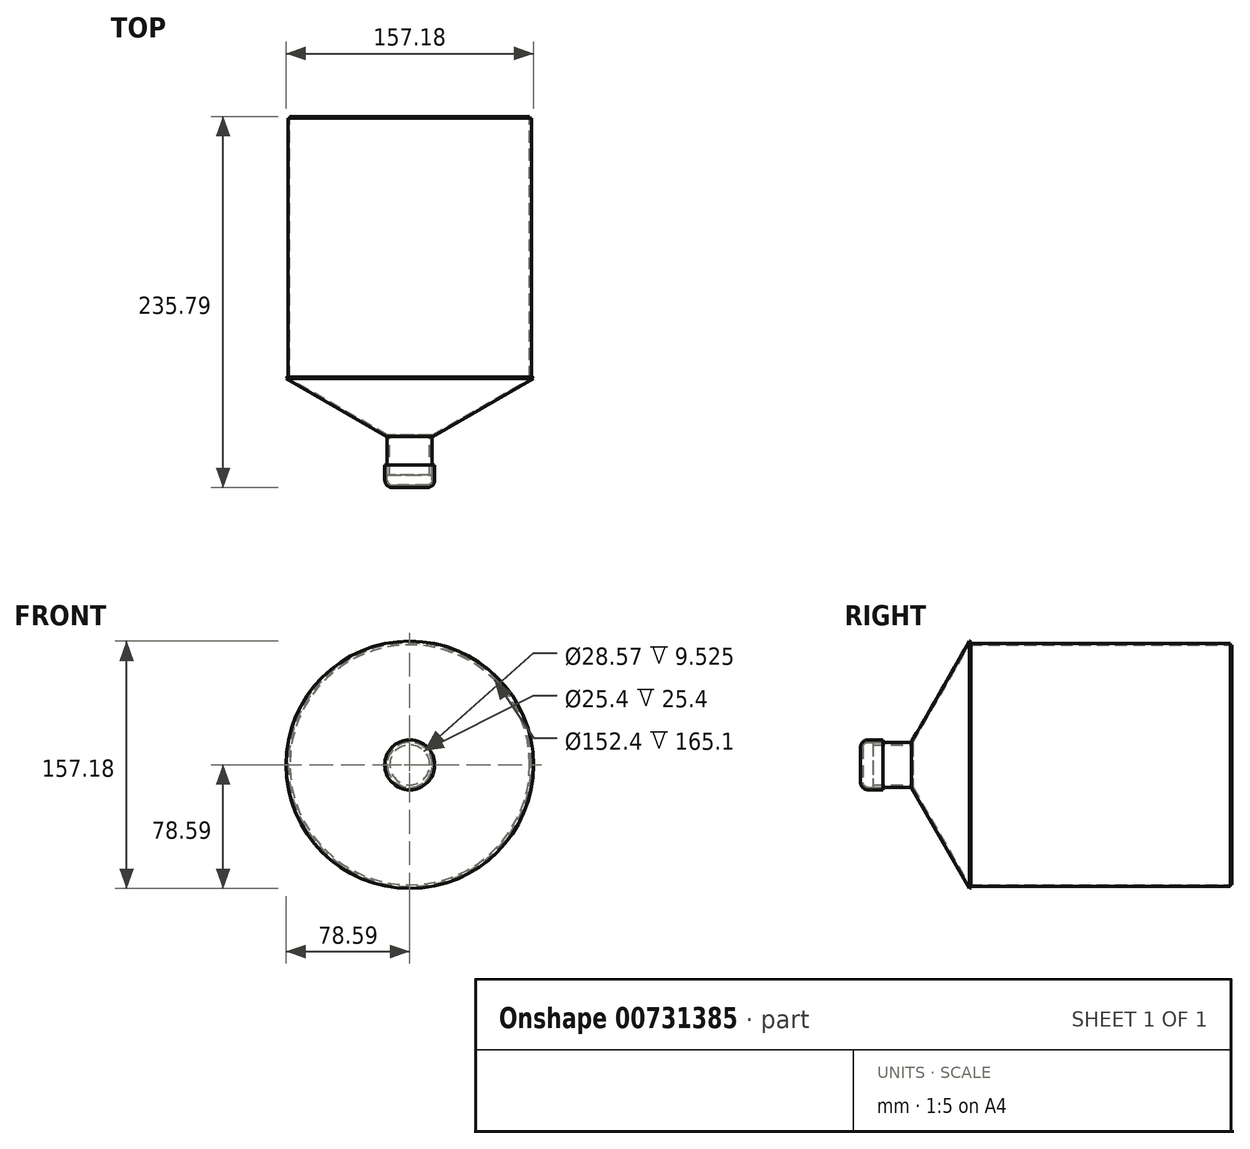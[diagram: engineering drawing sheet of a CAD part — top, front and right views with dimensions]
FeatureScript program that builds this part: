
annotation { "Feature Type Name" : "Feature", "Feature Type Description" : "" }
export const myFeature = defineFeature(function(context is Context, id is Id, definition is map)
    precondition{}
    {
        {
            var Q0;
            Q0=qCreatedBy(makeId("Front.planeOp"),FACE);
            var sketch = newSketch(context, id + "F0", { "sketchPlane" : qUnion([Q0])});
            skCircle(sketch, "E0", {"center": v(0, 0) * mm, "radius": 76.2 * mm});
            skCircle(sketch, "E1.0", {"center": v(0, 0) * mm, "radius": 77.22 * mm});
            skSolve(sketch);
        }
        {
            var Q0;
            Q0 = qSketchRegion(id + "F0", true);
            extrude(context, id + "F1", {"entities" : qUnion([Q0]), "depth" : 165.1 * mm, "offsetDistance" : 25.4 * mm});
        }
        {
            var Q0;
            Q0=makeQuery(id+"F0.imprint","IMPRINT",FACE,{"disambiguationData":[TD([[makeQuery(id+"F0.imprint","IMPRINT",EDGE,{"derivedFrom":sQuery(id+"F0.wireOp",EDGE,"E0")}),1.0]])]});
            extrude(context, id + "F2", {"entities" : qUnion([Q0]), "oppositeDirection" : true, "depth" : 1.02 * mm, "offsetDistance" : 25.4 * mm});
        }
        {
            var Q0;
            Q0=qCreatedBy(makeId("Right.planeOp"),FACE);
            var sketch = newSketch(context, id + "F3", { "sketchPlane" : qUnion([Q0])});
            skLineSegment(sketch, "E2", {"start": v(0, 0) * mm, "end": v(-195.69, 0) * mm, "construction": true});
            skLineSegment(sketch, "E3", {"start": v(-164.6, 78.08) * mm, "end": v(-201.43, 14.29) * mm});
            skPoint(sketch, "E4", {"position": v(-165.1, 77.22) * mm});
            skLineSegment(sketch, "E5.0", {"start": v(-165.48, 78.59) * mm, "end": v(-202.31, 14.8) * mm});
            skLineSegment(sketch, "E6", {"start": v(-202.31, 14.8) * mm, "end": v(-201.43, 14.29) * mm});
            skLineSegment(sketch, "E7", {"start": v(-165.48, 78.59) * mm, "end": v(-164.6, 78.08) * mm});
            skSolve(sketch);
        }
        {
            var Q0;
            Q0 = qSketchRegion(id + "F3", true);
            var Q1;
            Q1=sQuery(id+"F3.wireOp",EDGE,"E2");
            revolve(context, id + "F4", {"surfaceOperationType" : NewSurfaceOperationType.NEW, "entities" : qUnion([Q0]), "axis" : qUnion([Q1]), "revolveType" : RevolveType.FULL});
        }
        {
            var Q0;
            Q0=qCreatedBy(makeId("Right.planeOp"),FACE);
            var sketch = newSketch(context, id + "F5", { "sketchPlane" : qUnion([Q0])});
            skLineSegment(sketch, "E8", {"start": v(-1.93, 0) * mm, "end": v(-255.52, 0) * mm, "construction": true});
            skLineSegment(sketch, "E9", {"start": v(-201.43, 14.29) * mm, "end": v(-226.83, 14.29) * mm});
            skPoint(sketch, "E10", {"position": v(-201.43, 14.29) * mm});
            skLineSegment(sketch, "E11.0", {"start": v(-201.43, 12.7) * mm, "end": v(-226.83, 12.7) * mm});
            skLineSegment(sketch, "E12", {"start": v(-201.43, 12.7) * mm, "end": v(-201.43, 14.29) * mm});
            skLineSegment(sketch, "E13", {"start": v(-226.83, 14.29) * mm, "end": v(-226.83, 12.7) * mm});
            skSolve(sketch);
        }
        {
            var Q0;
            Q0 = qSketchRegion(id + "F5", true);
            var Q1;
            Q1=sQuery(id+"F5.wireOp",EDGE,"E8");
            revolve(context, id + "F6", {"surfaceOperationType" : NewSurfaceOperationType.NEW, "entities" : qUnion([Q0]), "axis" : qUnion([Q1]), "revolveType" : RevolveType.FULL});
        }
        {
            var Q0;
            Q0=qCreatedBy(makeId("Right.planeOp"),FACE);
            var sketch = newSketch(context, id + "F7", { "sketchPlane" : qUnion([Q0])});
            skLineSegment(sketch, "E14", {"start": v(0, 0) * mm, "end": v(-294.61, 0) * mm, "construction": true});
            skLineSegment(sketch, "E15", {"start": v(-220.48, 14.29) * mm, "end": v(-230, 14.29) * mm});
            skLineSegment(sketch, "E16", {"start": v(-233.18, 11.11) * mm, "end": v(-233.18, 0) * mm});
            skPoint(sketch, "E17.visualSharp", {"position": v(-233.18, 14.29) * mm});
            skArc(sketch, "E17.filletArc", {"start": v(-230, 14.29) * mm, "mid": v(-232.25, 13.36) * mm, "end": v(-233.18, 11.11) * mm});
            skLineSegment(sketch, "E18.0", {"start": v(-234.77, 11.11) * mm, "end": v(-234.77, 0) * mm});
            skArc(sketch, "E18.1", {"start": v(-230, 15.87) * mm, "mid": v(-233.37, 14.48) * mm, "end": v(-234.77, 11.11) * mm});
            skLineSegment(sketch, "E18.2", {"start": v(-220.48, 15.87) * mm, "end": v(-230, 15.87) * mm});
            skLineSegment(sketch, "E19", {"start": v(-220.48, 15.87) * mm, "end": v(-220.48, 14.29) * mm});
            skLineSegment(sketch, "E20", {"start": v(-234.77, 0) * mm, "end": v(-233.18, 0) * mm});
            skSolve(sketch);
        }
        {
            var Q0;
            Q0 = qSketchRegion(id + "F7", true);
            var Q1;
            Q1=sQuery(id+"F7.wireOp",EDGE,"E14");
            revolve(context, id + "F8", {"surfaceOperationType" : NewSurfaceOperationType.NEW, "entities" : qUnion([Q0]), "axis" : qUnion([Q1]), "revolveType" : RevolveType.FULL});
        }
    });
